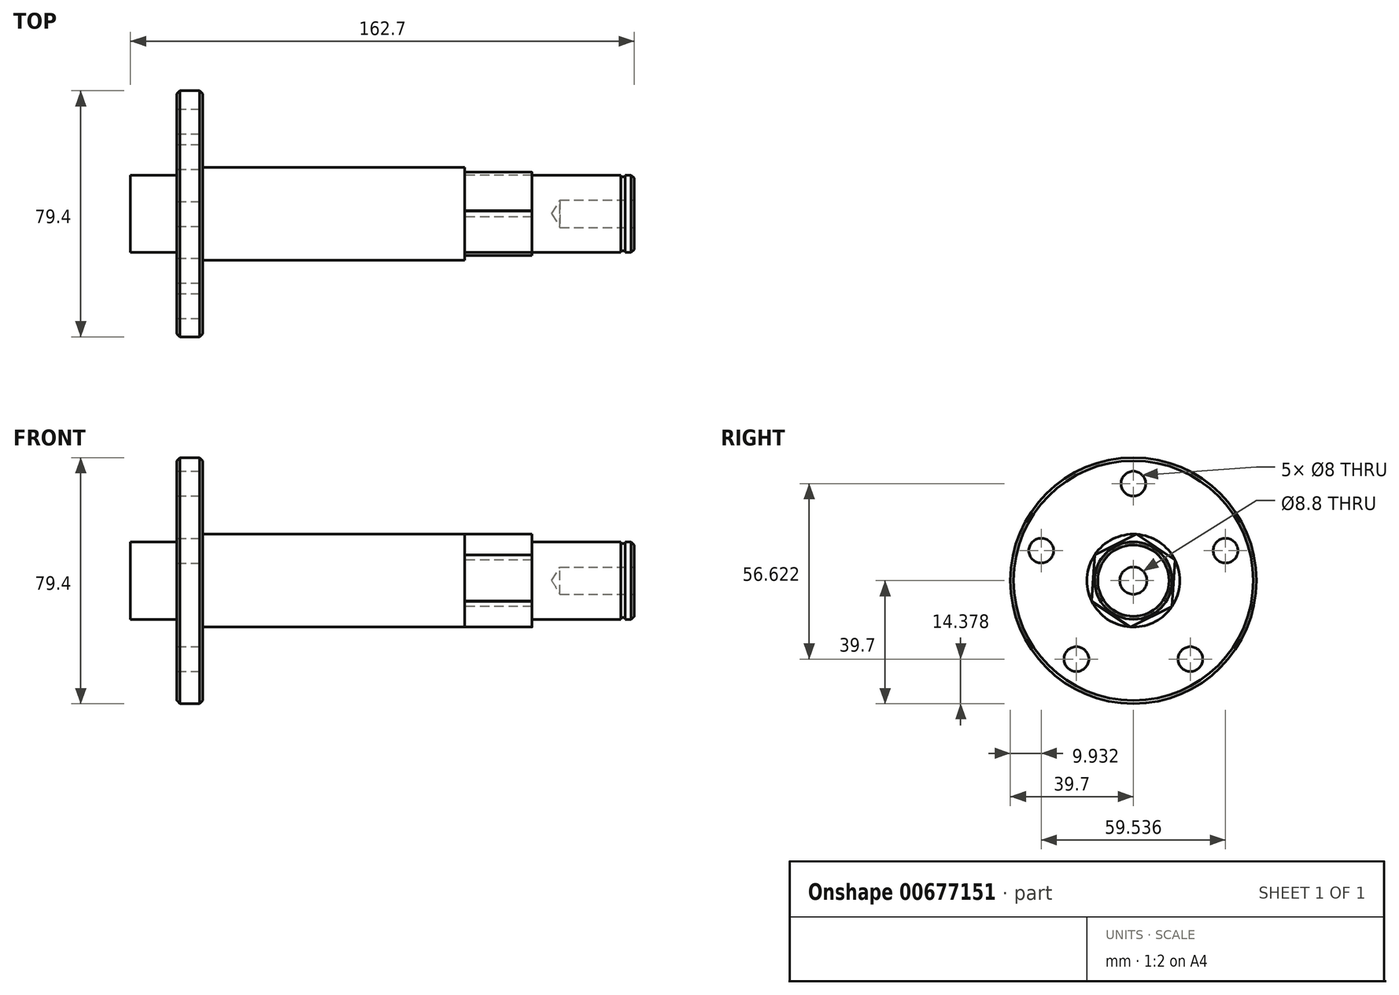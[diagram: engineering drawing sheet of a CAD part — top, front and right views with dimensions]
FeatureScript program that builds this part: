
annotation { "Feature Type Name" : "Feature", "Feature Type Description" : "" }
export const myFeature = defineFeature(function(context is Context, id is Id, definition is map)
    precondition{}
    {
        {
            var Q0;
            Q0=qCreatedBy(makeId("Front.planeOp"),FACE);
            var sketch = newSketch(context, id + "F0", { "sketchPlane" : qUnion([Q0])});
            skLineSegment(sketch, "E0", {"start": v(0, 0) * mm, "end": v(0, 12.5) * mm});
            skLineSegment(sketch, "E1", {"start": v(0, 12.5) * mm, "end": v(15, 12.5) * mm});
            skLineSegment(sketch, "E2", {"start": v(15, 12.5) * mm, "end": v(15, 39.7) * mm});
            skLineSegment(sketch, "E3", {"start": v(15, 39.7) * mm, "end": v(23.3, 39.7) * mm});
            skLineSegment(sketch, "E4", {"start": v(23.3, 39.7) * mm, "end": v(23.3, 15) * mm});
            skLineSegment(sketch, "E5", {"start": v(23.3, 15) * mm, "end": v(107.9, 15) * mm});
            skLineSegment(sketch, "E6", {"start": v(107.9, 15) * mm, "end": v(107.9, 0) * mm});
            skLineSegment(sketch, "E7", {"start": v(107.9, 0) * mm, "end": v(0, 0) * mm});
            skSolve(sketch);
        }
        {
            var Q0;
            Q0=makeQuery(id+"F0.imprint","IMPRINT",FACE,{"disambiguationData":[TD([[makeQuery(id+"F0.imprint","IMPRINT",EDGE,{"derivedFrom":sQuery(id+"F0.wireOp",EDGE,"E0")}),-1.0]])]});
            var Q1;
            Q1=sQuery(id+"F0.wireOp",EDGE,"E7");
            revolve(context, id + "F1", {"surfaceOperationType" : NewSurfaceOperationType.NEW, "entities" : qUnion([Q0]), "axis" : qUnion([Q1]), "revolveType" : RevolveType.FULL});
        }
        {
            var Q0;
            Q0=makeQuery(id+"F1.opRevolve","SWEPT_FACE",FACE,{"disambiguationData":[OSD([sQuery(id+"F0.wireOp",EDGE,"E6")])]});
            var sketch = newSketch(context, id + "F2", { "sketchPlane" : qUnion([Q0])});
            skCircle(sketch, "E8.cCircle", {"center": v(0, 0) * mm, "radius": 13 * mm, "construction": true});
            skLineSegment(sketch, "E8.0", {"start": v(12.48, -8.33) * mm, "end": v(-0.98, -14.98) * mm});
            skLineSegment(sketch, "E8.1", {"start": v(-0.98, -14.98) * mm, "end": v(-13.46, -6.64) * mm});
            skLineSegment(sketch, "E8.2", {"start": v(-13.46, -6.64) * mm, "end": v(-12.48, 8.33) * mm});
            skLineSegment(sketch, "E8.3", {"start": v(-12.48, 8.33) * mm, "end": v(0.98, 14.98) * mm});
            skLineSegment(sketch, "E8.4", {"start": v(0.98, 14.98) * mm, "end": v(13.46, 6.64) * mm});
            skLineSegment(sketch, "E8.5", {"start": v(13.46, 6.64) * mm, "end": v(12.48, -8.33) * mm});
            skPoint(sketch, "E8.0.midPoint", {"position": v(5.75, -11.66) * mm});
            skSolve(sketch);
        }
        {
            var Q0;
            {var subQ0=sQuery(id+"F2.wireOp",EDGE,"E8.0");var subQ1=makeQuery(id+"F1.opRevolve","SWEPT_EDGE",EDGE,{"disambiguationData":[OSD([sQuery(id+"F0.wireOp",EDGE,"E5"),sQuery(id+"F0.wireOp",EDGE,"E6")])]});var subQ13=makeQuery(id+"F2.imprint","INTERSECT",VERTEX,{"disambiguationData":[OD(0.0)],"derivedFrom":[subQ1,subQ0]});Q0=makeQuery(id+"F2.imprint","IMPRINT",FACE,{"disambiguationData":[TD([[makeQuery(id+"F2.imprint","IMPRINT",EDGE,{"disambiguationData":[TD([[subQ13,-1.0]])],"derivedFrom":subQ0}),-1.0]])]});}
            extrude(context, id + "F3", {"entities" : qUnion([Q0]), "depth" : 21.8 * mm, "offsetDistance" : 25 * mm});
        }
        {
            var Q0;
            Q0=makeQuery(id+"F3.opExtrude","CAP_FACE",FACE,{"disambiguationData":[OSD([sQuery(id+"F0.wireOp",VERTEX,"E6.start"),sQuery(id+"F2.wireOp",EDGE,"E8.0"),sQuery(id+"F2.wireOp",EDGE,"E8.1"),sQuery(id+"F2.wireOp",EDGE,"E8.2"),sQuery(id+"F2.wireOp",EDGE,"E8.3"),sQuery(id+"F2.wireOp",EDGE,"E8.4"),sQuery(id+"F2.wireOp",EDGE,"E8.5")])],"isStart":false});
            var sketch = newSketch(context, id + "F4", { "sketchPlane" : qUnion([Q0])});
            skCircle(sketch, "E9", {"center": v(0, 0) * mm, "radius": 12.5 * mm});
            skSolve(sketch);
        }
        {
            var Q0;
            Q0=makeQuery(id+"F4.imprint","IMPRINT",FACE,{"disambiguationData":[TD([[makeQuery(id+"F4.imprint","IMPRINT",EDGE,{"derivedFrom":sQuery(id+"F4.wireOp",EDGE,"E9")}),1.0]])]});
            extrude(context, id + "F5", {"entities" : qUnion([Q0]), "operationType" : NewBodyOperationType.ADD, "depth" : 33 * mm, "offsetDistance" : 25 * mm});
        }
        {
            var Q0;
            Q0=makeQuery(id+"F1.opRevolve","SWEPT_EDGE",EDGE,{"disambiguationData":[OSD([sQuery(id+"F0.wireOp",VERTEX,"E0.end")])]});
            var Q1;
            Q1=makeQuery(id+"F5.opExtrude","CAP_EDGE",EDGE,{"disambiguationData":[OSD([sQuery(id+"F4.wireOp",EDGE,"E9")])],"isStart":false});
            chamfer(context, id + "F6", {"entities" : qUnion([Q0, Q1]), "width" : 1 * mm, "tangentPropagation" : true});
        }
        {
            var Q0;
            Q0=makeQuery(id+"F5.opExtrude","CAP_FACE",FACE,{"disambiguationData":[OSD([sQuery(id+"F4.wireOp",EDGE,"E9")])],"isStart":false});
            cPlane(context, id + "F7", {"entities" : qUnion([Q0]), "cplaneType" : CPlaneType.OFFSET, "offset" : 3 * mm, "oppositeDirection" : true, "width" : 150 * mm, "height" : 150 * mm});
        }
        {
            var Q0;
            Q0=qCreatedBy(id+"F7.planeOp",FACE);
            var sketch = newSketch(context, id + "F8", { "sketchPlane" : qUnion([Q0])});
            skCircle(sketch, "E10", {"center": v(0, 0) * mm, "radius": 11.95 * mm});
            skCircle(sketch, "E11", {"center": v(0, 0) * mm, "radius": 15 * mm});
            skSolve(sketch);
        }
        {
            var Q0;
            Q0=makeQuery(id+"F8.imprint","IMPRINT",FACE,{"disambiguationData":[TD([[makeQuery(id+"F8.imprint","IMPRINT",EDGE,{"derivedFrom":sQuery(id+"F8.wireOp",EDGE,"E10")}),-1.0]])]});
            extrude(context, id + "F9", {"entities" : qUnion([Q0]), "operationType" : NewBodyOperationType.REMOVE, "oppositeDirection" : true, "depth" : 1.3 * mm, "offsetDistance" : 25 * mm});
        }
        {
            var Q0;
            Q0=makeQuery(id+"F1.opRevolve","SWEPT_FACE",FACE,{"disambiguationData":[OSD([sQuery(id+"F0.wireOp",EDGE,"E4")])]});
            var sketch = newSketch(context, id + "F10", { "sketchPlane" : qUnion([Q0])});
            skCircle(sketch, "E12", {"center": v(0, 31.3) * mm, "radius": 4 * mm});
            skCircle(sketch, "E13.1.0", {"center": v(-29.77, 9.67) * mm, "radius": 4 * mm});
            skCircle(sketch, "E13.2.0", {"center": v(-18.4, -25.32) * mm, "radius": 4 * mm});
            skCircle(sketch, "E13.3.0", {"center": v(18.4, -25.32) * mm, "radius": 4 * mm});
            skCircle(sketch, "E13.4.0", {"center": v(29.77, 9.67) * mm, "radius": 4 * mm});
            skPoint(sketch, "E13.center", {"position": v(0, 0) * mm});
            skSolve(sketch);
        }
        {
            var Q0;
            Q0=makeQuery(id+"F10.imprint","IMPRINT",FACE,{"disambiguationData":[TD([[makeQuery(id+"F10.imprint","IMPRINT",EDGE,{"derivedFrom":sQuery(id+"F10.wireOp",EDGE,"E12")}),1.0]])]});
            var Q1;
            Q1=makeQuery(id+"F10.imprint","IMPRINT",FACE,{"disambiguationData":[TD([[makeQuery(id+"F10.imprint","IMPRINT",EDGE,{"derivedFrom":sQuery(id+"F10.wireOp",EDGE,"E13.4.0")}),1.0]])]});
            var Q2;
            Q2=makeQuery(id+"F10.imprint","IMPRINT",FACE,{"disambiguationData":[TD([[makeQuery(id+"F10.imprint","IMPRINT",EDGE,{"derivedFrom":sQuery(id+"F10.wireOp",EDGE,"E13.3.0")}),1.0]])]});
            var Q3;
            Q3=makeQuery(id+"F10.imprint","IMPRINT",FACE,{"disambiguationData":[TD([[makeQuery(id+"F10.imprint","IMPRINT",EDGE,{"derivedFrom":sQuery(id+"F10.wireOp",EDGE,"E13.2.0")}),1.0]])]});
            var Q4;
            Q4=makeQuery(id+"F10.imprint","IMPRINT",FACE,{"disambiguationData":[TD([[makeQuery(id+"F10.imprint","IMPRINT",EDGE,{"derivedFrom":sQuery(id+"F10.wireOp",EDGE,"E13.1.0")}),1.0]])]});
            extrude(context, id + "F11", {"entities" : qUnion([Q0, Q1, Q2, Q3, Q4]), "operationType" : NewBodyOperationType.REMOVE, "endBound" : BoundingType.UP_TO_NEXT, "oppositeDirection" : true, "depth" : 25 * mm, "offsetDistance" : 25 * mm});
        }
        {
            var Q0;
            Q0=makeQuery(id+"F5.opExtrude","CAP_FACE",FACE,{"disambiguationData":[OSD([sQuery(id+"F4.wireOp",EDGE,"E9")])],"isStart":false});
            var sketch = newSketch(context, id + "F12", { "sketchPlane" : qUnion([Q0])});
            skPoint(sketch, "E14", {"position": v(0, 0) * mm});
            skSolve(sketch);
        }
        {
            var Q0;
            Q0=sQuery(id+"F12.wireOp",VERTEX,"E14");
            var Q1;
            Q1=makeQuery(id+"F3.opExtrude","SWEPT_BODY",BODY,{"disambiguationData":[OSD([sQuery(id+"F0.wireOp",EDGE,"E5"),sQuery(id+"F0.wireOp",EDGE,"E6"),sQuery(id+"F2.wireOp",EDGE,"E8.0"),sQuery(id+"F2.wireOp",EDGE,"E8.1"),sQuery(id+"F2.wireOp",EDGE,"E8.2"),sQuery(id+"F2.wireOp",EDGE,"E8.3"),sQuery(id+"F2.wireOp",EDGE,"E8.4"),sQuery(id+"F2.wireOp",EDGE,"E8.5")])]});
            hole(context, id + "F13", {"style" : HoleStyle.SIMPLE, "endStyle" : HoleEndStyle.BLIND, "standardTappedOrClearance" : lookupTablePath({ "standard" : "ISO", "fit" : "Normal", "size" : "M8", "type" : "Clearance" }), "standardBlindInLast" : lookupTablePath({ "fit" : "Standard", "standard" : "ISO", "size" : "M8", "type" : "Clearance" }), "holeDiameter" : 8.8 * mm, "majorDiameter" : 5 * mm, "holeDepth" : 24 * mm, "isTappedThrough" : true, "tappedDepth" : 20 * mm, "tapClearance" : 2, "locations" : qUnion([Q0]), "scope" : qUnion([Q1])});
        }
        {
            var Q0;
            Q0=makeQuery(id+"F1.opRevolve","SWEPT_EDGE",EDGE,{"disambiguationData":[OSD([sQuery(id+"F0.wireOp",EDGE,"E2"),sQuery(id+"F0.wireOp",EDGE,"E3")])]});
            var Q1;
            Q1=makeQuery(id+"F1.opRevolve","SWEPT_EDGE",EDGE,{"disambiguationData":[OSD([sQuery(id+"F0.wireOp",EDGE,"E3"),sQuery(id+"F0.wireOp",EDGE,"E4")])]});
            chamfer(context, id + "F14", {"entities" : qUnion([Q0, Q1]), "width" : 1 * mm, "tangentPropagation" : true});
        }
    });
